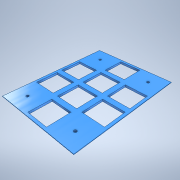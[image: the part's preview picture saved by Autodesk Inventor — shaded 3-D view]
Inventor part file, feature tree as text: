
AUTODESK INVENTOR PART (.ipt)
format: ipt  version: 2021 (Build 250183000, 183)  size: 243,712 bytes
history: native  units: mm
features: extrude x5, sketch x5
ambient origin geometry x8: Origin, YZ Plane, XZ Plane, XY Plane, X Axis, Y Axis, Z Axis, Center Point
bodies: Solid1 (feature_tree)
feature tree (10):
  extrude  "Extrusion4"  Depth=5.0mm
  extrude  "Extrusion1"  Depth=200.0mm
  extrude  "Extrusion5"  Depth=150.0mm
  extrude  "Extrusion6"  Depth=1.0mm TaperAngle=0.0deg
  extrude  "Extrusion7"  Depth=100.0mm
  sketch  "Sketch4"  dims[d70=40.0mm d72=50.0mm d73=30.0mm d75=50.0mm d78=5.0mm d79=-5.235988mm]
  sketch  "Sketch9"  dims[d86=150.0mm d87=200.0mm]
  sketch  "Sketch10"  dims[d94=3.0mm d95=0.0mm d96=150.0mm]
  sketch  "Sketch13"  dims[d97=200.0mm d98=1.0mm d99=0.0mm]
  sketch  "Sketch16"  dims[d109=5.0mm d110=20.0mm d112=100.0mm d113=20.0mm d115=150.0mm d118=3.0mm d119=0.0mm d120=40.0mm d121=40.0mm d122=20.0mm d124=50.0mm d125=30.0mm d127=50.0mm d130=20.0mm d132=50.0mm d133=10.0mm d135=10.0mm d137=20.0mm d139=50.0mm d140=10.0mm d142=10.0mm d144=0.0mm d145=0.0mm d82=0.5mm d83=0.872665mm d84=0.5mm d85=0.872665mm d123=0.872665mm]
